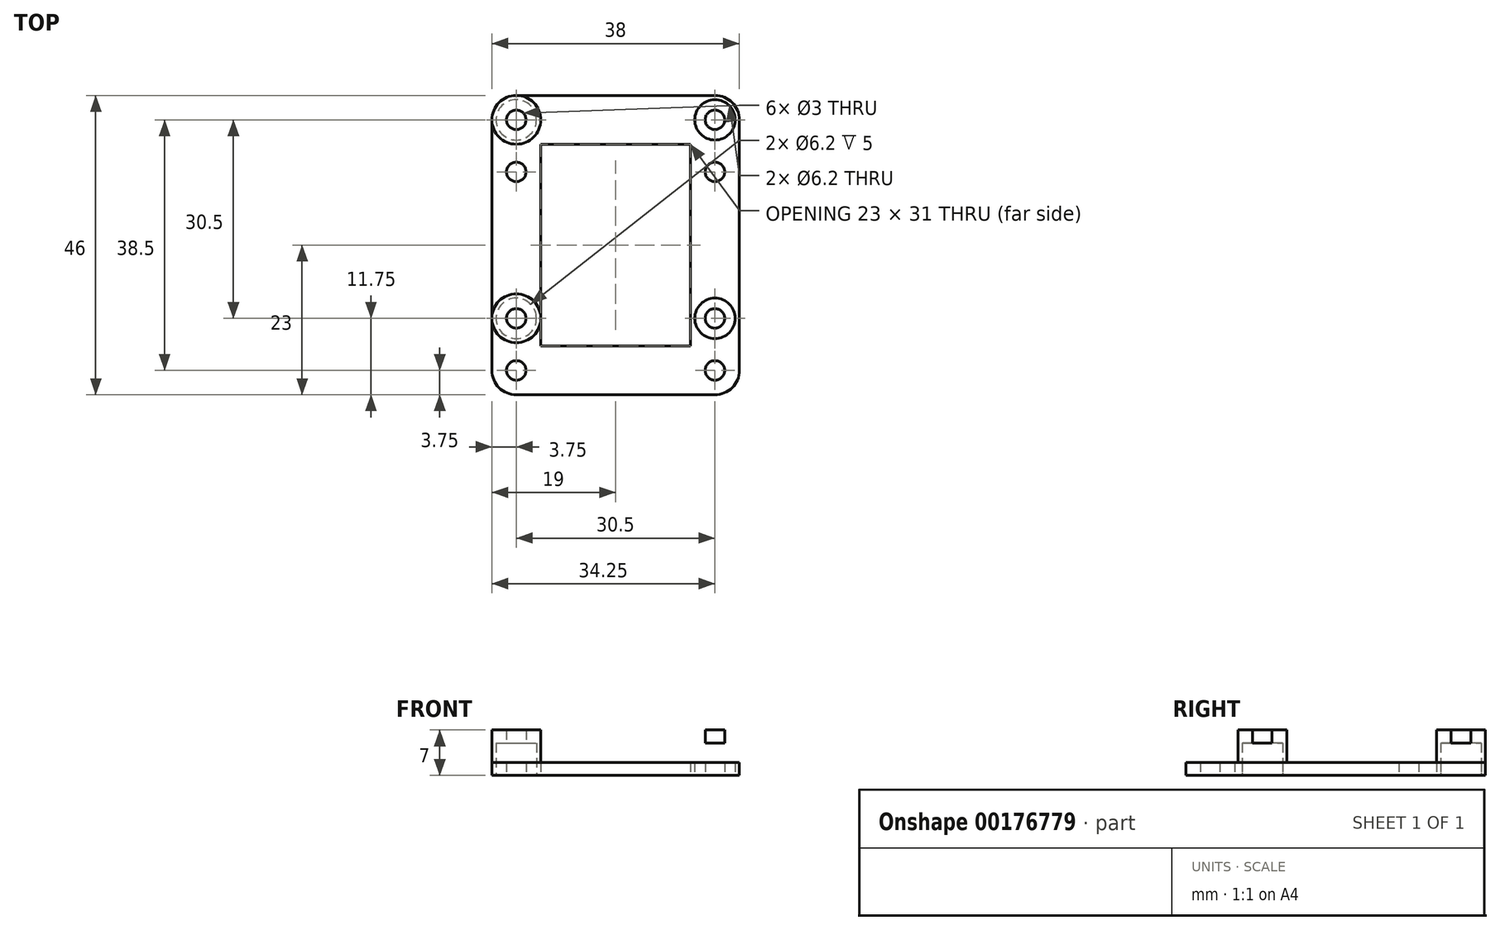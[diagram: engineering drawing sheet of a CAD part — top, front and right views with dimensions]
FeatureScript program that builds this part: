
annotation { "Feature Type Name" : "Feature", "Feature Type Description" : "" }
export const myFeature = defineFeature(function(context is Context, id is Id, definition is map)
    precondition{}
    {
        {
            assignVariable(context, id + "F0", {"name" : "railWidth", "anyValue" : 7.5});
        }
        {
            assignVariable(context, id + "F1", {"name" : "zOffset", "anyValue" : 5});
        }
        {
            assignVariable(context, id + "F2", {"name" : "defaultThickness", "anyValue" : 2});
        }
        {
            var Q0;
            Q0=qCreatedBy(makeId("Top.planeOp"),FACE);
            var sketch = newSketch(context, id + "F3", { "sketchPlane" : qUnion([Q0])});
            skLineSegment(sketch, "E0.bottom", {"start": v(-11.5, 15.5) * mm, "end": v(11.5, 15.5) * mm});
            skLineSegment(sketch, "E0.top", {"start": v(-11.5, -15.5) * mm, "end": v(11.5, -15.5) * mm});
            skLineSegment(sketch, "E0.left", {"start": v(-11.5, 15.5) * mm, "end": v(-11.5, -15.5) * mm});
            skLineSegment(sketch, "E0.right", {"start": v(11.5, 15.5) * mm, "end": v(11.5, -15.5) * mm});
            skPoint(sketch, "E0.middle", {"position": v(0, 0) * mm});
            skLineSegment(sketch, "E1.bottom", {"start": v(-19, 23) * mm, "end": v(19, 23) * mm});
            skLineSegment(sketch, "E1.top", {"start": v(-19, -23) * mm, "end": v(19, -23) * mm});
            skLineSegment(sketch, "E1.left", {"start": v(-19, 23) * mm, "end": v(-19, -23) * mm});
            skLineSegment(sketch, "E1.right", {"start": v(19, 23) * mm, "end": v(19, -23) * mm});
            skCircle(sketch, "E2", {"center": v(-15.25, -19.25) * mm, "radius": 1.5 * mm});
            skCircle(sketch, "E3", {"center": v(-15.25, -11.25) * mm, "radius": 1.5 * mm});
            skCircle(sketch, "E4", {"center": v(-15.25, 11.25) * mm, "radius": 1.5 * mm});
            skCircle(sketch, "E5", {"center": v(-15.25, 19.25) * mm, "radius": 1.5 * mm});
            skCircle(sketch, "E6.MirrorC", {"center": v(15.25, -19.25) * mm, "radius": 1.5 * mm});
            skCircle(sketch, "E7.MirrorC", {"center": v(15.25, -11.25) * mm, "radius": 1.5 * mm});
            skCircle(sketch, "E8.MirrorC", {"center": v(15.25, 11.25) * mm, "radius": 1.5 * mm});
            skCircle(sketch, "E9.MirrorC", {"center": v(15.25, 19.25) * mm, "radius": 1.5 * mm});
            skLineSegment(sketch, "E10", {"start": v(-15.25, -11.25) * mm, "end": v(-15.25, 11.25) * mm, "construction": true});
            skLineSegment(sketch, "E11", {"start": v(15.25, 11.25) * mm, "end": v(15.25, -11.25) * mm, "construction": true});
            skSolve(sketch);
        }
        {
            var Q0;
            Q0 = qSketchRegion(id + "F3", true);
            extrude(context, id + "F4", {"entities" : qUnion([Q0]), "depth" : (getVariable(context, 'defaultThickness')) * mm});
        }
        {
            var Q0;
            Q0=makeQuery(id+"F4.opExtrude","CAP_FACE",FACE,{"disambiguationData":[OSD([sQuery(id+"F3.wireOp",EDGE,"E0.bottom"),sQuery(id+"F3.wireOp",EDGE,"E0.top"),sQuery(id+"F3.wireOp",EDGE,"E0.left"),sQuery(id+"F3.wireOp",EDGE,"E0.right"),sQuery(id+"F3.wireOp",EDGE,"E1.bottom"),sQuery(id+"F3.wireOp",EDGE,"E1.top"),sQuery(id+"F3.wireOp",EDGE,"E1.left"),sQuery(id+"F3.wireOp",EDGE,"E1.right"),sQuery(id+"F3.wireOp",EDGE,"E2"),sQuery(id+"F3.wireOp",EDGE,"E3"),sQuery(id+"F3.wireOp",EDGE,"E4"),sQuery(id+"F3.wireOp",EDGE,"E5"),sQuery(id+"F3.wireOp",EDGE,"E6.MirrorC"),sQuery(id+"F3.wireOp",EDGE,"E7.MirrorC"),sQuery(id+"F3.wireOp",EDGE,"E8.MirrorC"),sQuery(id+"F3.wireOp",EDGE,"E9.MirrorC")])],"isStart":false});
            var sketch = newSketch(context, id + "F5", { "sketchPlane" : qUnion([Q0])});
            skCircle(sketch, "E12", {"center": v(-15.25, 19.25) * mm, "radius": 3.75 * mm});
            skCircle(sketch, "E13", {"center": v(-15.25, 19.25) * mm, "radius": 1.5 * mm});
            skCircle(sketch, "E14", {"center": v(-15.25, 11.25) * mm, "radius": 3.75 * mm});
            skCircle(sketch, "E15", {"center": v(-15.25, 11.25) * mm, "radius": 1.5 * mm});
            skCircle(sketch, "E16", {"center": v(-15.25, -11.25) * mm, "radius": 3.75 * mm});
            skCircle(sketch, "E17", {"center": v(-15.25, -11.25) * mm, "radius": 1.5 * mm});
            skCircle(sketch, "E18", {"center": v(-15.25, -19.25) * mm, "radius": 3.75 * mm});
            skCircle(sketch, "E19", {"center": v(-15.25, -19.25) * mm, "radius": 1.5 * mm});
            skCircle(sketch, "E20.MirrorC", {"center": v(15.25, 19.25) * mm, "radius": 1.5 * mm});
            skCircle(sketch, "E21.MirrorC", {"center": v(15.25, 19.25) * mm, "radius": 3.75 * mm});
            skCircle(sketch, "E22.MirrorC", {"center": v(15.25, 11.25) * mm, "radius": 1.5 * mm});
            skCircle(sketch, "E23.MirrorC", {"center": v(15.25, 11.25) * mm, "radius": 3.75 * mm});
            skCircle(sketch, "E24.MirrorC", {"center": v(15.25, -11.25) * mm, "radius": 1.5 * mm});
            skCircle(sketch, "E25.MirrorC", {"center": v(15.25, -11.25) * mm, "radius": 3.75 * mm});
            skCircle(sketch, "E26.MirrorC", {"center": v(15.25, -19.25) * mm, "radius": 1.5 * mm});
            skCircle(sketch, "E27.MirrorC", {"center": v(15.25, -19.25) * mm, "radius": 3.75 * mm});
            skSolve(sketch);
        }
        {
            var Q0;
            Q0=makeQuery(id+"F5.imprint","IMPRINT",FACE,{"disambiguationData":[TD([[makeQuery(id+"F5.imprint","IMPRINT",EDGE,{"derivedFrom":sQuery(id+"F5.wireOp",EDGE,"E13")}),-1.0]])]});
            var Q1;
            Q1=makeQuery(id+"F5.imprint","IMPRINT",FACE,{"disambiguationData":[TD([[makeQuery(id+"F5.imprint","IMPRINT",EDGE,{"derivedFrom":sQuery(id+"F5.wireOp",EDGE,"E20.MirrorC")}),1.0]])]});
            var Q2;
            Q2=makeQuery(id+"F5.imprint","IMPRINT",FACE,{"disambiguationData":[TD([[makeQuery(id+"F5.imprint","IMPRINT",EDGE,{"derivedFrom":sQuery(id+"F5.wireOp",EDGE,"E24.MirrorC")}),1.0]])]});
            var Q3;
            Q3=makeQuery(id+"F5.imprint","IMPRINT",FACE,{"disambiguationData":[TD([[makeQuery(id+"F5.imprint","IMPRINT",EDGE,{"derivedFrom":sQuery(id+"F5.wireOp",EDGE,"E17")}),-1.0]])]});
            extrude(context, id + "F6", {"entities" : qUnion([Q0, Q1, Q2, Q3]), "operationType" : NewBodyOperationType.ADD, "depth" : (getVariable(context, 'zOffset')) * mm});
        }
        {
            var Q0;
            Q0=makeQuery(id+"F4.opExtrude","SWEPT_EDGE",EDGE,{"disambiguationData":[OSD([sQuery(id+"F3.wireOp",EDGE,"E1.bottom"),sQuery(id+"F3.wireOp",EDGE,"E1.left")])]});
            var Q1;
            Q1=makeQuery(id+"F4.opExtrude","SWEPT_EDGE",EDGE,{"disambiguationData":[OSD([sQuery(id+"F3.wireOp",EDGE,"E1.top"),sQuery(id+"F3.wireOp",EDGE,"E1.left")])]});
            var Q2;
            Q2=makeQuery(id+"F4.opExtrude","SWEPT_EDGE",EDGE,{"disambiguationData":[OSD([sQuery(id+"F3.wireOp",EDGE,"E1.top"),sQuery(id+"F3.wireOp",EDGE,"E1.right")])]});
            var Q3;
            Q3=makeQuery(id+"F4.opExtrude","SWEPT_EDGE",EDGE,{"disambiguationData":[OSD([sQuery(id+"F3.wireOp",EDGE,"E1.bottom"),sQuery(id+"F3.wireOp",EDGE,"E1.right")])]});
            fillet(context, id + "F7", {"entities" : qUnion([Q0, Q1, Q2, Q3]), "radius" : (getVariable(context, 'railWidth') / 2) * mm, "tangentPropagation" : true, "allowEdgeOverflow" : false});
        }
        {
            var Q0;
            Q0=makeQuery(id+"F4.opExtrude","CAP_FACE",FACE,{"disambiguationData":[OSD([sQuery(id+"F3.wireOp",EDGE,"E0.bottom"),sQuery(id+"F3.wireOp",EDGE,"E0.top"),sQuery(id+"F3.wireOp",EDGE,"E0.left"),sQuery(id+"F3.wireOp",EDGE,"E0.right"),sQuery(id+"F3.wireOp",EDGE,"E1.bottom"),sQuery(id+"F3.wireOp",EDGE,"E1.top"),sQuery(id+"F3.wireOp",EDGE,"E1.left"),sQuery(id+"F3.wireOp",EDGE,"E1.right"),sQuery(id+"F3.wireOp",EDGE,"E2"),sQuery(id+"F3.wireOp",EDGE,"E3"),sQuery(id+"F3.wireOp",EDGE,"E4"),sQuery(id+"F3.wireOp",EDGE,"E5"),sQuery(id+"F3.wireOp",EDGE,"E6.MirrorC"),sQuery(id+"F3.wireOp",EDGE,"E7.MirrorC"),sQuery(id+"F3.wireOp",EDGE,"E8.MirrorC"),sQuery(id+"F3.wireOp",EDGE,"E9.MirrorC")])],"isStart":true});
            var sketch = newSketch(context, id + "F8", { "sketchPlane" : qUnion([Q0])});
            skCircle(sketch, "E28", {"center": v(-15.25, 11.25) * mm, "radius": 3.1 * mm});
            skCircle(sketch, "E29", {"center": v(15.25, 11.25) * mm, "radius": 3.1 * mm});
            skCircle(sketch, "E30", {"center": v(15.25, -19.25) * mm, "radius": 3.1 * mm});
            skCircle(sketch, "E31", {"center": v(-15.25, -19.25) * mm, "radius": 3.1 * mm});
            skSolve(sketch);
        }
        {
            var Q0;
            Q0 = qSketchRegion(id + "F8", true);
            extrude(context, id + "F9", {"entities" : qUnion([Q0]), "operationType" : NewBodyOperationType.REMOVE, "oppositeDirection" : true, "depth" : (getVariable(context, 'zOffset')) * mm});
        }
    });
